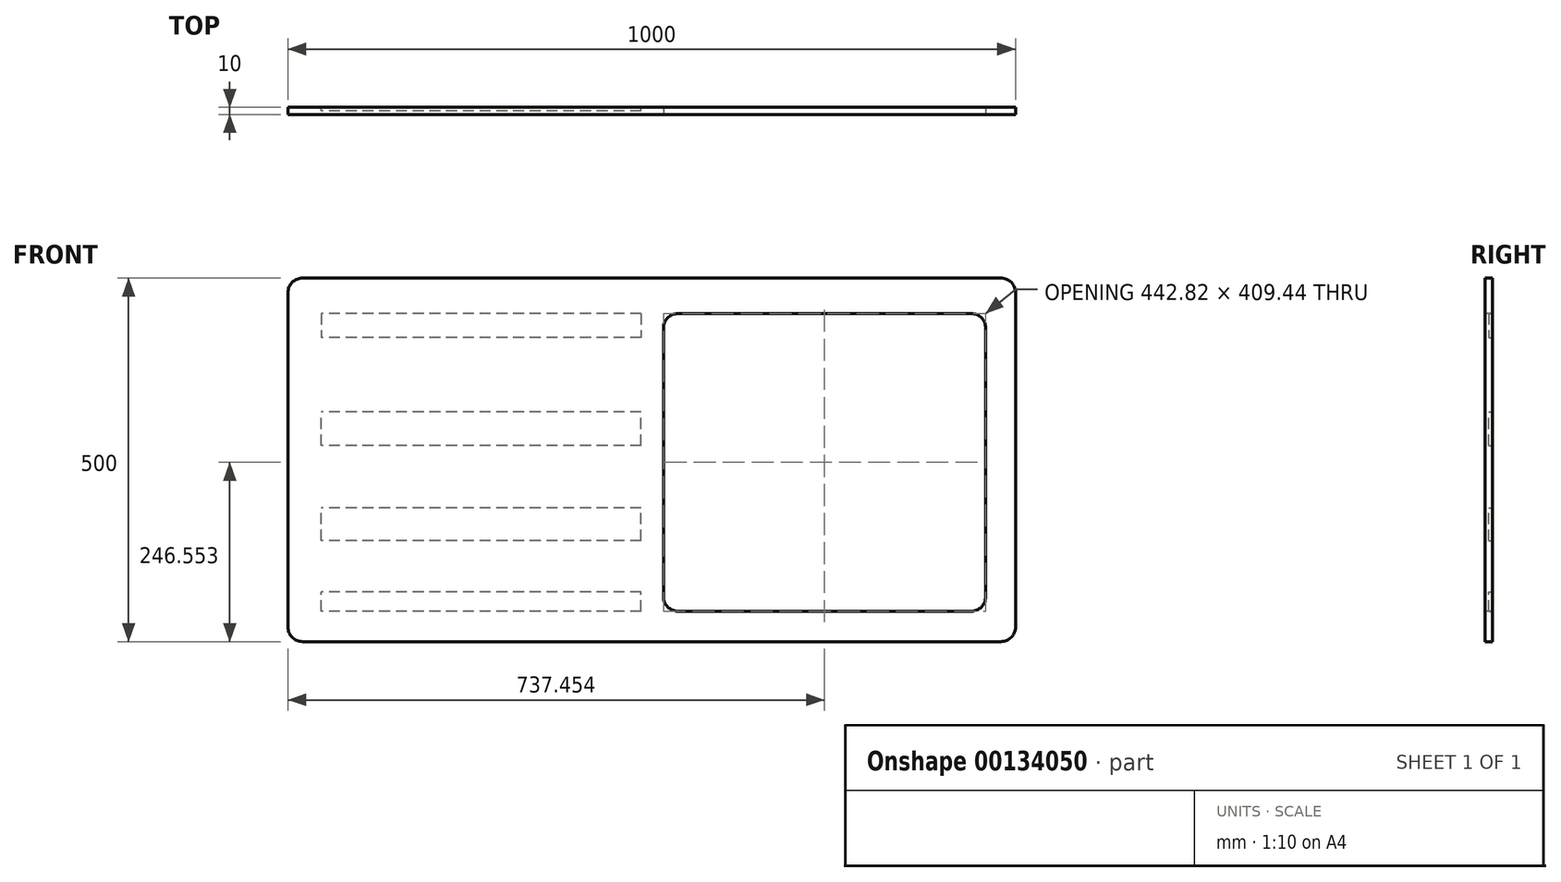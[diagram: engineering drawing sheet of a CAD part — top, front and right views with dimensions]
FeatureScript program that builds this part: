
annotation { "Feature Type Name" : "Feature", "Feature Type Description" : "" }
export const myFeature = defineFeature(function(context is Context, id is Id, definition is map)
    precondition{}
    {
        {
            var Q0;
            Q0=qCreatedBy(makeId("Front.planeOp"),FACE);
            var sketch = newSketch(context, id + "F0", { "sketchPlane" : qUnion([Q0])});
            skLineSegment(sketch, "E0.bottom", {"start": v(-465.4, 316.36) * mm, "end": v(494.6, 316.36) * mm});
            skLineSegment(sketch, "E0.top", {"start": v(-465.4, -183.64) * mm, "end": v(494.6, -183.64) * mm});
            skLineSegment(sketch, "E0.left", {"start": v(-485.4, 296.36) * mm, "end": v(-485.4, -163.64) * mm});
            skLineSegment(sketch, "E0.right", {"start": v(514.6, 296.36) * mm, "end": v(514.6, -163.64) * mm});
            skPoint(sketch, "E1.visualSharp", {"position": v(514.6, 316.36) * mm});
            skArc(sketch, "E1.filletArc", {"start": v(514.6, 296.36) * mm, "mid": v(508.73, 310.5) * mm, "end": v(494.6, 316.36) * mm});
            skPoint(sketch, "E2.visualSharp", {"position": v(514.6, -183.64) * mm});
            skArc(sketch, "E2.filletArc", {"start": v(494.6, -183.64) * mm, "mid": v(508.73, -177.78) * mm, "end": v(514.6, -163.64) * mm});
            skPoint(sketch, "E3.visualSharp", {"position": v(-485.4, -183.64) * mm});
            skArc(sketch, "E3.filletArc", {"start": v(-485.4, -163.64) * mm, "mid": v(-479.55, -177.78) * mm, "end": v(-465.4, -183.64) * mm});
            skPoint(sketch, "E4.visualSharp", {"position": v(-485.4, 316.36) * mm});
            skArc(sketch, "E4.filletArc", {"start": v(-465.4, 316.36) * mm, "mid": v(-479.55, 310.5) * mm, "end": v(-485.4, 296.36) * mm});
            skSolve(sketch);
        }
        {
            var Q0;
            Q0=makeQuery(id+"F0.imprint","IMPRINT",FACE,{"disambiguationData":[TD([[makeQuery(id+"F0.imprint","IMPRINT",EDGE,{"derivedFrom":sQuery(id+"F0.wireOp",EDGE,"E0.bottom")}),-1.0]])]});
            extrude(context, id + "F1", {"entities" : qUnion([Q0]), "depth" : 10 * mm});
        }
        {
            var Q0;
            Q0=makeQuery(id+"F1.opExtrude","CAP_FACE",FACE,{"disambiguationData":[OSD([sQuery(id+"F0.wireOp",EDGE,"E0.bottom"),sQuery(id+"F0.wireOp",EDGE,"E0.top"),sQuery(id+"F0.wireOp",EDGE,"E0.left"),sQuery(id+"F0.wireOp",EDGE,"E0.right"),sQuery(id+"F0.wireOp",EDGE,"E1.filletArc"),sQuery(id+"F0.wireOp",EDGE,"E2.filletArc"),sQuery(id+"F0.wireOp",EDGE,"E3.filletArc"),sQuery(id+"F0.wireOp",EDGE,"E4.filletArc")])],"isStart":false});
            var sketch = newSketch(context, id + "F2", { "sketchPlane" : qUnion([Q0])});
            skLineSegment(sketch, "E5.bottom", {"start": v(50.64, 267.63) * mm, "end": v(453.45, 267.63) * mm});
            skLineSegment(sketch, "E5.top", {"start": v(50.64, -141.8) * mm, "end": v(453.45, -141.8) * mm});
            skLineSegment(sketch, "E5.left", {"start": v(30.64, 247.63) * mm, "end": v(30.64, -121.8) * mm});
            skLineSegment(sketch, "E5.right", {"start": v(473.45, 247.63) * mm, "end": v(473.45, -121.8) * mm});
            skPoint(sketch, "E6.visualSharp", {"position": v(30.64, 267.63) * mm});
            skArc(sketch, "E6.filletArc", {"start": v(50.64, 267.63) * mm, "mid": v(36.5, 261.77) * mm, "end": v(30.64, 247.63) * mm});
            skPoint(sketch, "E7.visualSharp", {"position": v(473.45, -141.8) * mm});
            skArc(sketch, "E7.filletArc", {"start": v(453.45, -141.8) * mm, "mid": v(467.6, -135.95) * mm, "end": v(473.45, -121.8) * mm});
            skPoint(sketch, "E8.visualSharp", {"position": v(473.45, 267.63) * mm});
            skArc(sketch, "E8.filletArc", {"start": v(473.45, 247.63) * mm, "mid": v(467.6, 261.77) * mm, "end": v(453.45, 267.63) * mm});
            skPoint(sketch, "E9.visualSharp", {"position": v(30.64, -141.8) * mm});
            skArc(sketch, "E9.filletArc", {"start": v(30.64, -121.8) * mm, "mid": v(36.5, -135.95) * mm, "end": v(50.64, -141.8) * mm});
            skSolve(sketch);
        }
        {
            var Q0;
            Q0=makeQuery(id+"F2.imprint","IMPRINT",FACE,{"disambiguationData":[TD([[makeQuery(id+"F2.imprint","IMPRINT",EDGE,{"derivedFrom":sQuery(id+"F2.wireOp",EDGE,"E5.bottom")}),-1.0]])]});
            extrude(context, id + "F3", {"entities" : qUnion([Q0]), "operationType" : NewBodyOperationType.REMOVE, "oppositeDirection" : true, "depth" : 25 * mm});
        }
        {
            var Q0;
            Q0=makeQuery(id+"F1.opExtrude","CAP_FACE",FACE,{"disambiguationData":[OSD([sQuery(id+"F0.wireOp",EDGE,"E0.bottom"),sQuery(id+"F0.wireOp",EDGE,"E0.top"),sQuery(id+"F0.wireOp",EDGE,"E0.left"),sQuery(id+"F0.wireOp",EDGE,"E0.right"),sQuery(id+"F0.wireOp",EDGE,"E1.filletArc"),sQuery(id+"F0.wireOp",EDGE,"E2.filletArc"),sQuery(id+"F0.wireOp",EDGE,"E3.filletArc"),sQuery(id+"F0.wireOp",EDGE,"E4.filletArc")])],"isStart":true});
            var sketch = newSketch(context, id + "F4", { "sketchPlane" : qUnion([Q0])});
            skLineSegment(sketch, "E10.bottom", {"start": v(0, -141.8) * mm, "end": v(439.6, -141.8) * mm});
            skLineSegment(sketch, "E10.top", {"start": v(0, -115.34) * mm, "end": v(439.6, -115.34) * mm});
            skLineSegment(sketch, "E10.left", {"start": v(0, -141.8) * mm, "end": v(0, -115.34) * mm});
            skLineSegment(sketch, "E10.right", {"start": v(439.6, -141.8) * mm, "end": v(439.6, -115.34) * mm});
            skLineSegment(sketch, "E11.bottom", {"start": v(0, -44.72) * mm, "end": v(439.6, -44.72) * mm});
            skLineSegment(sketch, "E11.top", {"start": v(0, 0) * mm, "end": v(439.6, 0) * mm});
            skLineSegment(sketch, "E11.left", {"start": v(0, -44.72) * mm, "end": v(0, 0) * mm});
            skLineSegment(sketch, "E11.right", {"start": v(439.6, -44.72) * mm, "end": v(439.6, 0) * mm});
            skLineSegment(sketch, "E12.bottom", {"start": v(0, 86.18) * mm, "end": v(439.6, 86.18) * mm});
            skLineSegment(sketch, "E12.top", {"start": v(0, 132.43) * mm, "end": v(439.6, 132.43) * mm});
            skLineSegment(sketch, "E12.left", {"start": v(0, 86.18) * mm, "end": v(0, 132.43) * mm});
            skLineSegment(sketch, "E12.right", {"start": v(439.6, 86.18) * mm, "end": v(439.6, 132.43) * mm});
            skLineSegment(sketch, "E13.bottom", {"start": v(0, 267.63) * mm, "end": v(439.6, 267.63) * mm});
            skLineSegment(sketch, "E13.top", {"start": v(0, 234.56) * mm, "end": v(439.6, 234.56) * mm});
            skLineSegment(sketch, "E13.left", {"start": v(0, 267.63) * mm, "end": v(0, 234.56) * mm});
            skLineSegment(sketch, "E13.right", {"start": v(439.6, 267.63) * mm, "end": v(439.6, 234.56) * mm});
            skSolve(sketch);
        }
        {
            var Q0;
            Q0=makeQuery(id+"F4.imprint","IMPRINT",FACE,{"disambiguationData":[TD([[makeQuery(id+"F4.imprint","IMPRINT",EDGE,{"derivedFrom":sQuery(id+"F4.wireOp",EDGE,"E10.bottom")}),1.0]])]});
            var Q1;
            Q1=makeQuery(id+"F4.imprint","IMPRINT",FACE,{"disambiguationData":[TD([[makeQuery(id+"F4.imprint","IMPRINT",EDGE,{"derivedFrom":sQuery(id+"F4.wireOp",EDGE,"E11.bottom")}),1.0]])]});
            var Q2;
            Q2=makeQuery(id+"F4.imprint","IMPRINT",FACE,{"disambiguationData":[TD([[makeQuery(id+"F4.imprint","IMPRINT",EDGE,{"derivedFrom":sQuery(id+"F4.wireOp",EDGE,"E12.bottom")}),1.0]])]});
            var Q3;
            Q3=makeQuery(id+"F4.imprint","IMPRINT",FACE,{"disambiguationData":[TD([[makeQuery(id+"F4.imprint","IMPRINT",EDGE,{"derivedFrom":sQuery(id+"F4.wireOp",EDGE,"E13.bottom")}),-1.0]])]});
            extrude(context, id + "F5", {"entities" : qUnion([Q0, Q1, Q2, Q3]), "operationType" : NewBodyOperationType.REMOVE, "oppositeDirection" : true, "depth" : 5 * mm});
        }
    });
